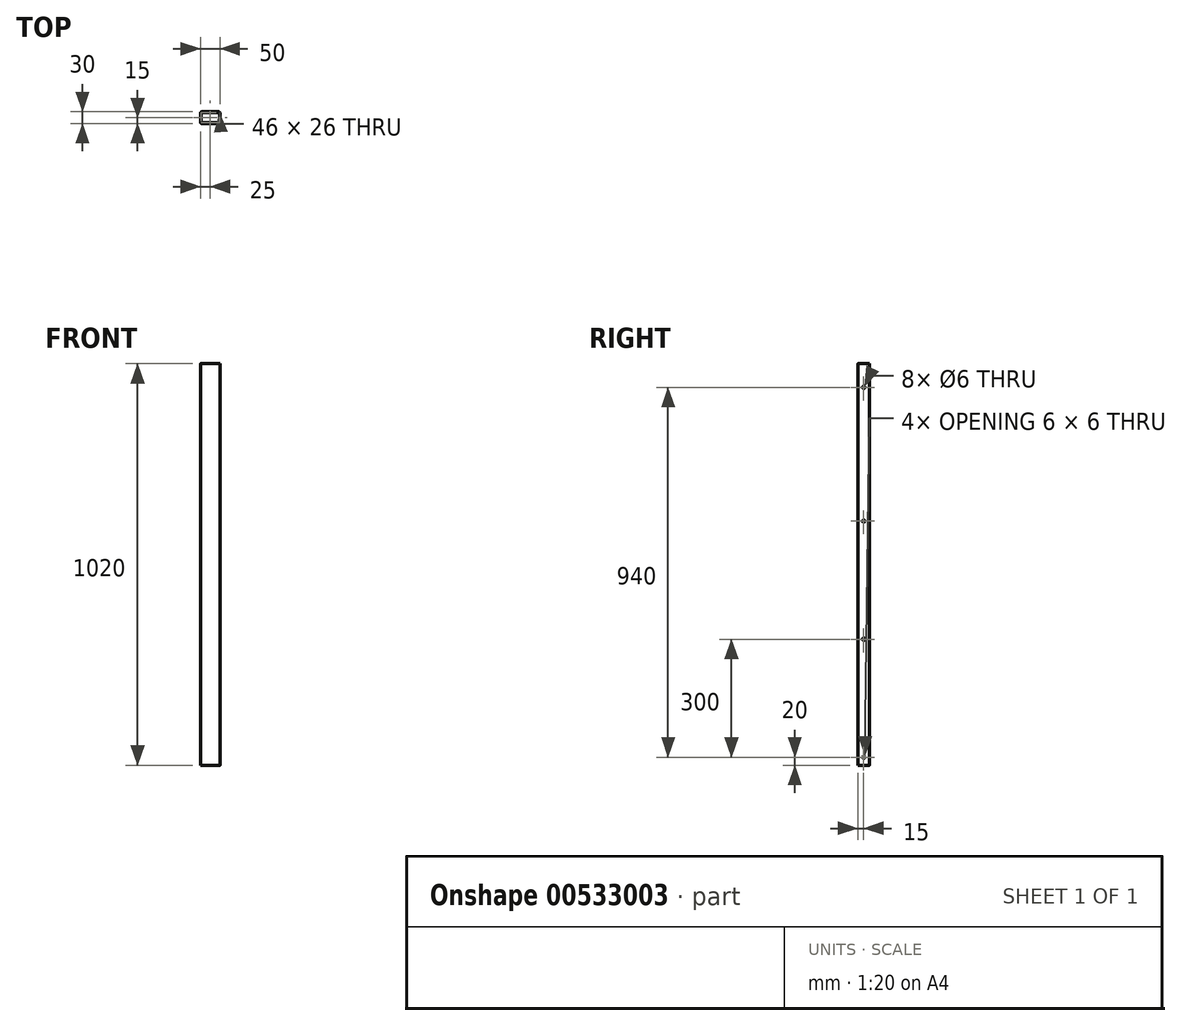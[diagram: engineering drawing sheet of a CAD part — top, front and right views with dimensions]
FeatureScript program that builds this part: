
annotation { "Feature Type Name" : "Feature", "Feature Type Description" : "" }
export const myFeature = defineFeature(function(context is Context, id is Id, definition is map)
    precondition{}
    {
        {
            var Q0;
            Q0=qCreatedBy(makeId("Top.planeOp"),FACE);
            var sketch = newSketch(context, id + "F0", { "sketchPlane" : qUnion([Q0])});
            skLineSegment(sketch, "E0.bottom", {"start": v(21.5, 15) * mm, "end": v(-21.5, 15) * mm});
            skLineSegment(sketch, "E0.top", {"start": v(21.5, -15) * mm, "end": v(-21.5, -15) * mm});
            skLineSegment(sketch, "E0.left", {"start": v(25, 11.5) * mm, "end": v(25, -11.5) * mm});
            skLineSegment(sketch, "E0.right", {"start": v(-25, 11.5) * mm, "end": v(-25, -11.5) * mm});
            skPoint(sketch, "E0.middle", {"position": v(0, 0) * mm});
            skLineSegment(sketch, "E1.bottom", {"start": v(23, -13) * mm, "end": v(-23, -13) * mm});
            skLineSegment(sketch, "E1.top", {"start": v(23, 13) * mm, "end": v(-23, 13) * mm});
            skLineSegment(sketch, "E1.left", {"start": v(23, -13) * mm, "end": v(23, 13) * mm});
            skLineSegment(sketch, "E1.right", {"start": v(-23, -13) * mm, "end": v(-23, 13) * mm});
            skPoint(sketch, "E2.visualSharp", {"position": v(-25, 15) * mm});
            skArc(sketch, "E2.filletArc", {"start": v(-21.5, 15) * mm, "mid": v(-23.97, 13.97) * mm, "end": v(-25, 11.5) * mm});
            skPoint(sketch, "E3.visualSharp", {"position": v(-25, -15) * mm});
            skArc(sketch, "E3.filletArc", {"start": v(-25, -11.5) * mm, "mid": v(-23.97, -13.97) * mm, "end": v(-21.5, -15) * mm});
            skPoint(sketch, "E4.visualSharp", {"position": v(25, -15) * mm});
            skArc(sketch, "E4.filletArc", {"start": v(21.5, -15) * mm, "mid": v(23.97, -13.97) * mm, "end": v(25, -11.5) * mm});
            skPoint(sketch, "E5.visualSharp", {"position": v(25, 15) * mm});
            skArc(sketch, "E5.filletArc", {"start": v(25, 11.5) * mm, "mid": v(23.97, 13.97) * mm, "end": v(21.5, 15) * mm});
            skSolve(sketch);
        }
        {
            var Q0;
            Q0=makeQuery(id+"F0.imprint","IMPRINT",FACE,{"disambiguationData":[TD([[makeQuery(id+"F0.imprint","IMPRINT",EDGE,{"derivedFrom":sQuery(id+"F0.wireOp",EDGE,"E0.bottom")}),1.0]])]});
            extrude(context, id + "F1", {"entities" : qUnion([Q0]), "depth" : 1020 * mm, "offsetDistance" : 25 * mm});
        }
        {
            var Q0;
            Q0=makeQuery(id+"F1.opExtrude","SWEPT_FACE",FACE,{"disambiguationData":[OSD([sQuery(id+"F0.wireOp",EDGE,"E0.left")])]});
            var sketch = newSketch(context, id + "F2", { "sketchPlane" : qUnion([Q0])});
            skPoint(sketch, "E6", {"position": v(0, 20) * mm});
            skPoint(sketch, "E7", {"position": v(0, 320) * mm});
            skPoint(sketch, "E8", {"position": v(0, 620) * mm});
            skPoint(sketch, "E9", {"position": v(0, 960) * mm});
            skSolve(sketch);
        }
        {
            var Q0;
            Q0=sQuery(id+"F2.wireOp",VERTEX,"E9");
            var Q1;
            Q1=sQuery(id+"F2.wireOp",VERTEX,"E8");
            var Q2;
            Q2=sQuery(id+"F2.wireOp",VERTEX,"E7");
            var Q3;
            Q3=sQuery(id+"F2.wireOp",VERTEX,"E6");
            var Q4;
            Q4=makeQuery(id+"F1.opExtrude","SWEPT_BODY",BODY,{"disambiguationData":[OSD([sQuery(id+"F0.wireOp",EDGE,"E0.bottom"),sQuery(id+"F0.wireOp",EDGE,"E0.top"),sQuery(id+"F0.wireOp",EDGE,"E0.left"),sQuery(id+"F0.wireOp",EDGE,"E0.right"),sQuery(id+"F0.wireOp",EDGE,"E1.bottom"),sQuery(id+"F0.wireOp",EDGE,"E1.top"),sQuery(id+"F0.wireOp",EDGE,"E1.left"),sQuery(id+"F0.wireOp",EDGE,"E1.right"),sQuery(id+"F0.wireOp",EDGE,"E2.filletArc"),sQuery(id+"F0.wireOp",EDGE,"E3.filletArc"),sQuery(id+"F0.wireOp",EDGE,"E4.filletArc"),sQuery(id+"F0.wireOp",EDGE,"E5.filletArc")])]});
            hole(context, id + "F3", {"style" : HoleStyle.SIMPLE, "endStyle" : HoleEndStyle.THROUGH, "holeDiameter" : 6 * mm, "majorDiameter" : 5 * mm, "isTappedThrough" : true, "tappedDepth" : 12 * mm, "tapClearance" : 3, "locations" : qUnion([Q0, Q1, Q2, Q3]), "scope" : qUnion([Q4])});
        }
    });
